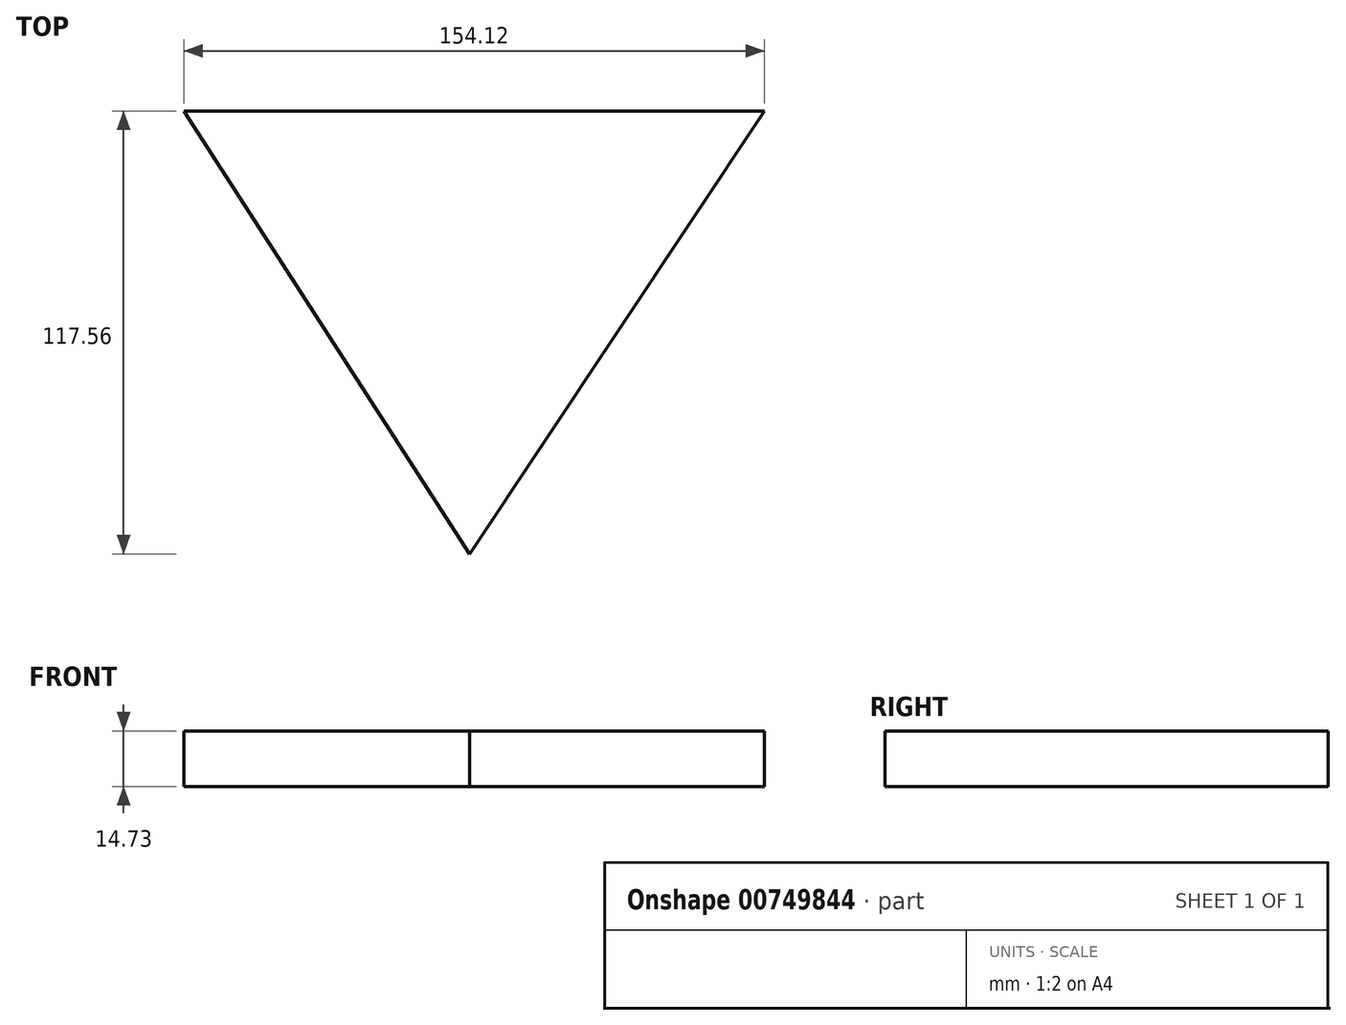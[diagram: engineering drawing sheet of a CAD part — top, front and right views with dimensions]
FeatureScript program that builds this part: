
annotation { "Feature Type Name" : "Feature", "Feature Type Description" : "" }
export const myFeature = defineFeature(function(context is Context, id is Id, definition is map)
    precondition{}
    {
        {
            var Q0;
            Q0=qCreatedBy(makeId("Top.planeOp"),FACE);
            var sketch = newSketch(context, id + "F0", { "sketchPlane" : qUnion([Q0])});
            skLineSegment(sketch, "E0", {"start": v(0, -76.24) * mm, "end": v(-75.88, 41.32) * mm});
            skLineSegment(sketch, "E1", {"start": v(-75.88, 41.32) * mm, "end": v(78.24, 41.32) * mm});
            skLineSegment(sketch, "E2", {"start": v(78.24, 41.32) * mm, "end": v(0, -76.24) * mm});
            skPoint(sketch, "E3", {"position": v(0, 29.98) * mm});
            skPoint(sketch, "E4", {"position": v(25.65, 29.98) * mm});
            skPoint(sketch, "E5", {"position": v(48.45, 29.98) * mm});
            skPoint(sketch, "E6", {"position": v(-22.91, 29.98) * mm});
            skPoint(sketch, "E7", {"position": v(-50.42, 29.98) * mm});
            skPoint(sketch, "E8", {"position": v(13, 0) * mm});
            skPoint(sketch, "E9", {"position": v(-10.37, 0) * mm});
            skPoint(sketch, "E10", {"position": v(-31.8, 0) * mm});
            skPoint(sketch, "E11", {"position": v(36.62, 0) * mm});
            skPoint(sketch, "E12", {"position": v(0, -19.13) * mm});
            skPoint(sketch, "E13", {"position": v(24.53, -19.13) * mm});
            skPoint(sketch, "E14", {"position": v(-19.51, -19.13) * mm});
            skPoint(sketch, "E15", {"position": v(11.34, -33.5) * mm});
            skPoint(sketch, "E16", {"position": v(-10.37, -33.5) * mm});
            skPoint(sketch, "E17", {"position": v(0, -54.04) * mm});
            skSolve(sketch);
        }
        {
            var Q0;
            Q0=makeQuery(id+"F0.imprint","IMPRINT",FACE,{"disambiguationData":[TD([[makeQuery(id+"F0.imprint","IMPRINT",EDGE,{"derivedFrom":sQuery(id+"F0.wireOp",EDGE,"E0")}),-1.0]])]});
            extrude(context, id + "F1", {"entities" : qUnion([Q0]), "depth" : 14.73 * mm, "offsetDistance" : 25.4 * mm});
        }
    });
